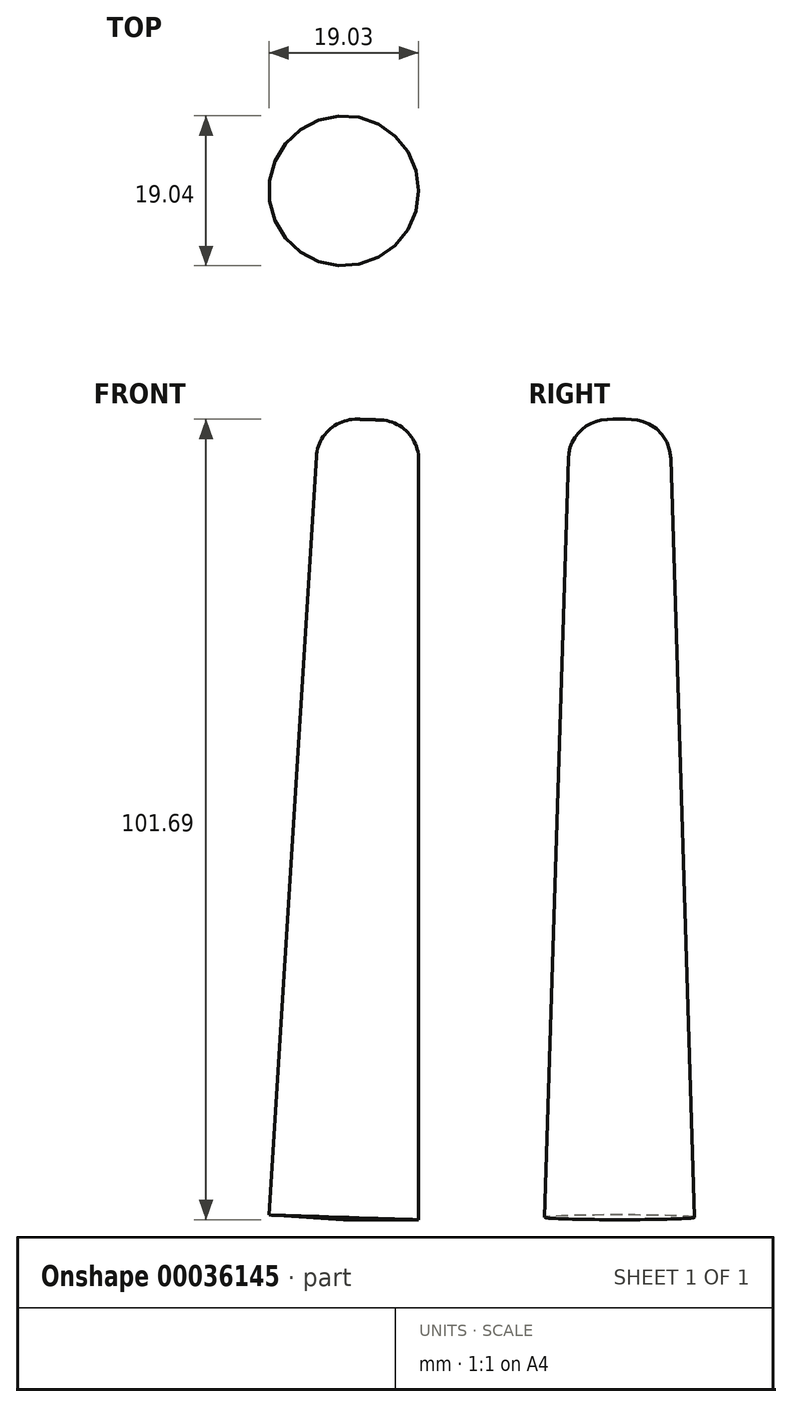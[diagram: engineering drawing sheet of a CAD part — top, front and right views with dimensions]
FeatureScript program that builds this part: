
annotation { "Feature Type Name" : "Feature", "Feature Type Description" : "" }
export const myFeature = defineFeature(function(context is Context, id is Id, definition is map)
    precondition{}
    {
        {
            var Q0;
            Q0=qCreatedBy(makeId("Front.planeOp"),FACE);
            var sketch = newSketch(context, id + "F0", { "sketchPlane" : qUnion([Q0])});
            skLineSegment(sketch, "E0", {"start": v(0, 0) * mm, "end": v(-9.53, 0) * mm});
            skLineSegment(sketch, "E1", {"start": v(-9.53, 0) * mm, "end": v(-6.35, 101.6) * mm});
            skLineSegment(sketch, "E2", {"start": v(-6.35, 101.6) * mm, "end": v(0, 101.6) * mm});
            skLineSegment(sketch, "E3", {"start": v(0, 101.6) * mm, "end": v(0, 0) * mm});
            skSolve(sketch);
        }
        {
            var Q0;
            Q0=makeQuery(id+"F0.imprint","IMPRINT",FACE,{"disambiguationData":[TD([[makeQuery(id+"F0.imprint","IMPRINT",EDGE,{"derivedFrom":sQuery(id+"F0.wireOp",EDGE,"E0")}),-1.0]])]});
            var Q1;
            Q1=sQuery(id+"F0.wireOp",EDGE,"E1");
            revolve(context, id + "F1", {"entities" : qUnion([Q0]), "axis" : qUnion([Q1]), "revolveType" : RevolveType.FULL, "oppositeDirection" : true});
        }
        {
            var Q0;
            Q0=makeQuery(id+"F1.opRevolve","SWEPT_EDGE",EDGE,{"disambiguationData":[OSD([sQuery(id+"F0.wireOp",EDGE,"E2"),sQuery(id+"F0.wireOp",EDGE,"E3")])]});
            fillet(context, id + "F2", {"entities" : qUnion([Q0]), "radius" : 5.08 * mm, "tangentPropagation" : true, "allowEdgeOverflow" : false});
        }
    });
